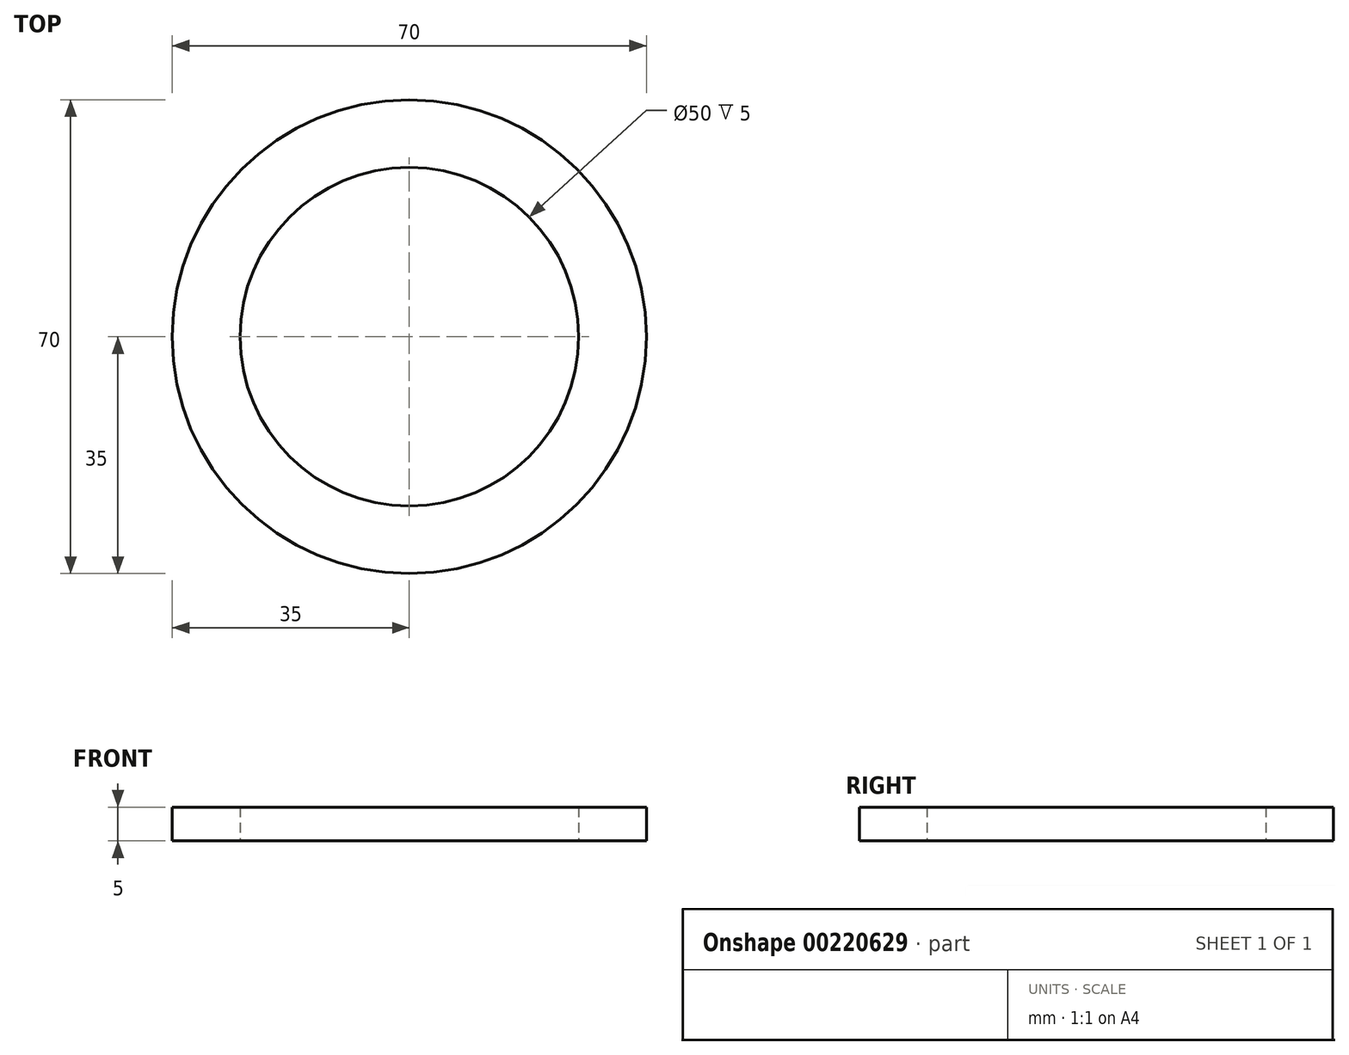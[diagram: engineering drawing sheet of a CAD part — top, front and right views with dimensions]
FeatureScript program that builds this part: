
annotation { "Feature Type Name" : "Feature", "Feature Type Description" : "" }
export const myFeature = defineFeature(function(context is Context, id is Id, definition is map)
    precondition{}
    {
        {
            var Q0;
            Q0=qCreatedBy(makeId("Top.planeOp"),FACE);
            var sketch = newSketch(context, id + "F0", { "sketchPlane" : qUnion([Q0])});
            skCircle(sketch, "E0", {"center": v(0, 0) * mm, "radius": 25 * mm});
            skCircle(sketch, "E1", {"center": v(0, 0) * mm, "radius": 35 * mm});
            skSolve(sketch);
        }
        {
            var Q0;
            Q0=makeQuery(id+"F0.imprint","IMPRINT",FACE,{"disambiguationData":[TD([[makeQuery(id+"F0.imprint","IMPRINT",EDGE,{"derivedFrom":sQuery(id+"F0.wireOp",EDGE,"E0")}),-1.0]])]});
            extrude(context, id + "F1", {"entities" : qUnion([Q0]), "depth" : 5 * mm});
        }
    });
